# Revit family: Тактильная керамическая плитка конус-шахматное расположение
name_source: partatom
category: Оборудование
revit_build: Autodesk Revit 2017 (Build: 20160225_1515(x64)
units: mm (PartAtom-declared; Revit-internal decimal feet)

## family parameters
Общий = Да
Основа = Грань
При загрузке вырезать с полостями = Да
Размер круглого соединителя = Использовать диаметр
Тип детали = Нормальный
Точка расчета площади = Нет

## types (1)
- Тактильная керамическая плитка конус/шахматное расположение
    ADSK_Код изделия = 10685-ZH
    ADSK_Материал наименование = Керамика, цвет желтый
    ADSK_Материал плитки = Керамическая плитка_Желтый
    ADSK_Наименование = Тактильная керамическая плитка конус/шахматное расположение
    ADSK_Размер_Высота рифа = 5 мм
    ADSK_Размер_Габариты = 300Х300
    ADSK_Размер_Длина = 300 мм
    ADSK_Размер_Толщина = 10 мм
    ADSK_Размер_Ширина = 300 мм
    ADSK_Тип рифов = Конусообразные рифы в шахматном порядке
    URL = http://tiflocentre.ru
    Изготовитель = ТИФЛОЦЕНТР «ВЕРТИКАЛЬ»
    Описание = Специалистами Тифлоцентра «Вертикаль» была разработана и изготовлена серия тактильной керамической плитки, которая соответствует всем российским стандартам. Такая плитка предназначена для укладки внутри помещений с высокой проходимостью. Конусообразные рифы в шахматном порядке "предупреждают" незрячего человека об опасности на пути и непреодолимой преграде. Желтый цвет плитки - служит контрастом к темной поверхности для людей с ограничениями зрения. 
Благодаря одинаковой структуре с керамогранитным покрытием, при монтаже такая плитка выглядит как законченное решение
Обладает антивандальными свойствами, поэтому отлично подходит для мест с большой проходимостью (вокзалы, аэропорты, метро)
Имеет универсальный размер – 300х300, подходящий большинству керамогранитных плит
Высокая прочность и долговечность покрытия обуславливаются толщиной керамической плитки – 10 мм
Легко поддается санитарной обработке, не теряя при этом своего первоначального вида
Специалистами Тифлоцентра «Вертикаль» была разработана и изготовлена серия тактильной керамической плитки, которая соответствует всем российским стандартам. Такая плитка предназначена для укладки внутри помещений с высокой проходимостью. Конусообразные рифы в шахматном порядке "предупреждают" незрячего человека об опасности на пути и непреодолимой преграде. Желтый цвет плитки - служит контрастом к темной поверхности для людей с ограничениями зрения. 
Благодаря одинаковой структуре с керамогранитным покрытием, при монтаже такая плитка выглядит как законченное решение
Обладает антивандальными свойствами, поэтому отлично подходит для мест с большой проходимостью (вокзалы, аэропорты, метро)
Имеет универсальный размер – 300х300, подходящий большинству керамогранитных плит
Высокая прочность и долговечность покрытия обуславливаются толщиной керамической плитки – 10 мм
Легко поддается санитарной обработке, не теряя при этом своего первоначального вида
    Отметка по умолчанию = 0 мм
    Применение = Помещение
    Стоимость = 1551 $
